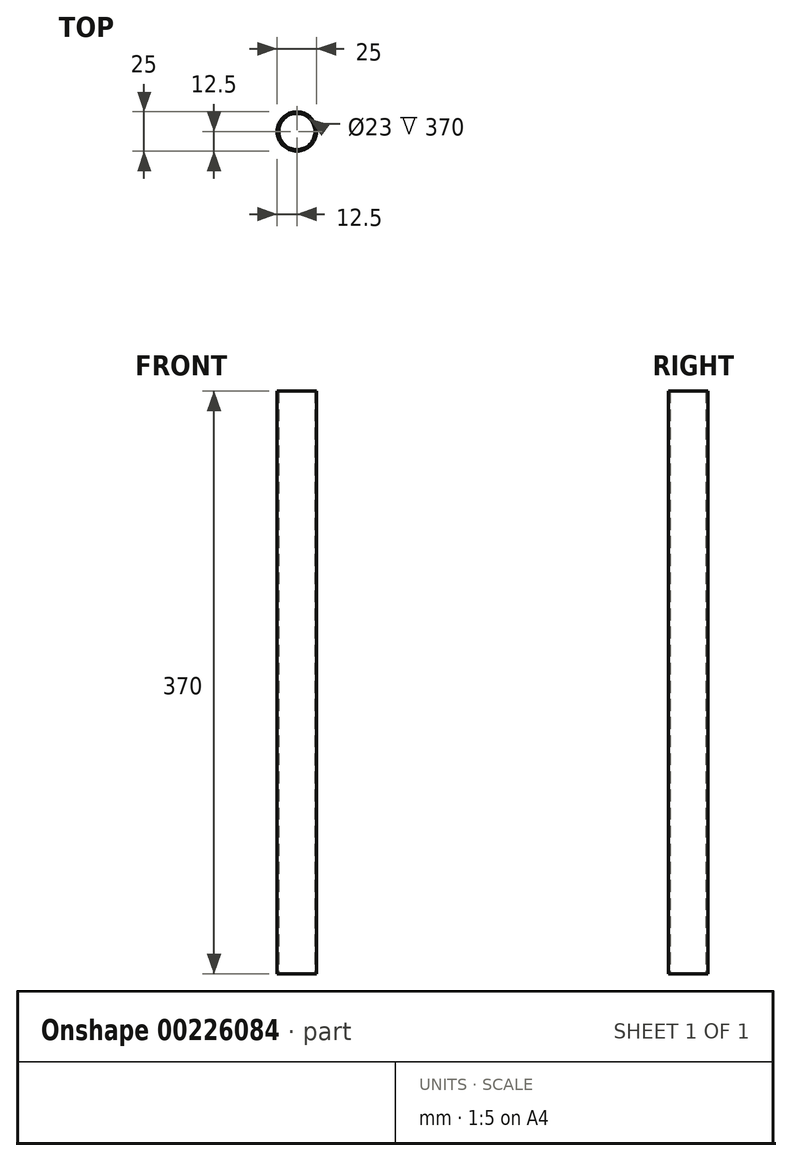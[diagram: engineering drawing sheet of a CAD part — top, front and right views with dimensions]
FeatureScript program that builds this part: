
annotation { "Feature Type Name" : "Feature", "Feature Type Description" : "" }
export const myFeature = defineFeature(function(context is Context, id is Id, definition is map)
    precondition{}
    {
        {
            var Q0;
            Q0=qCreatedBy(makeId("Top.planeOp"),FACE);
            var sketch = newSketch(context, id + "F0", { "sketchPlane" : qUnion([Q0])});
            skCircle(sketch, "E0", {"center": v(0, 0) * mm, "radius": 12.5 * mm});
            skCircle(sketch, "E1", {"center": v(0, 0) * mm, "radius": 11.5 * mm});
            skSolve(sketch);
        }
        {
            var Q0;
            Q0 = qSketchRegion(id + "F0", true);
            extrude(context, id + "F1", {"entities" : qUnion([Q0]), "depth" : 370 * mm});
        }
    });
